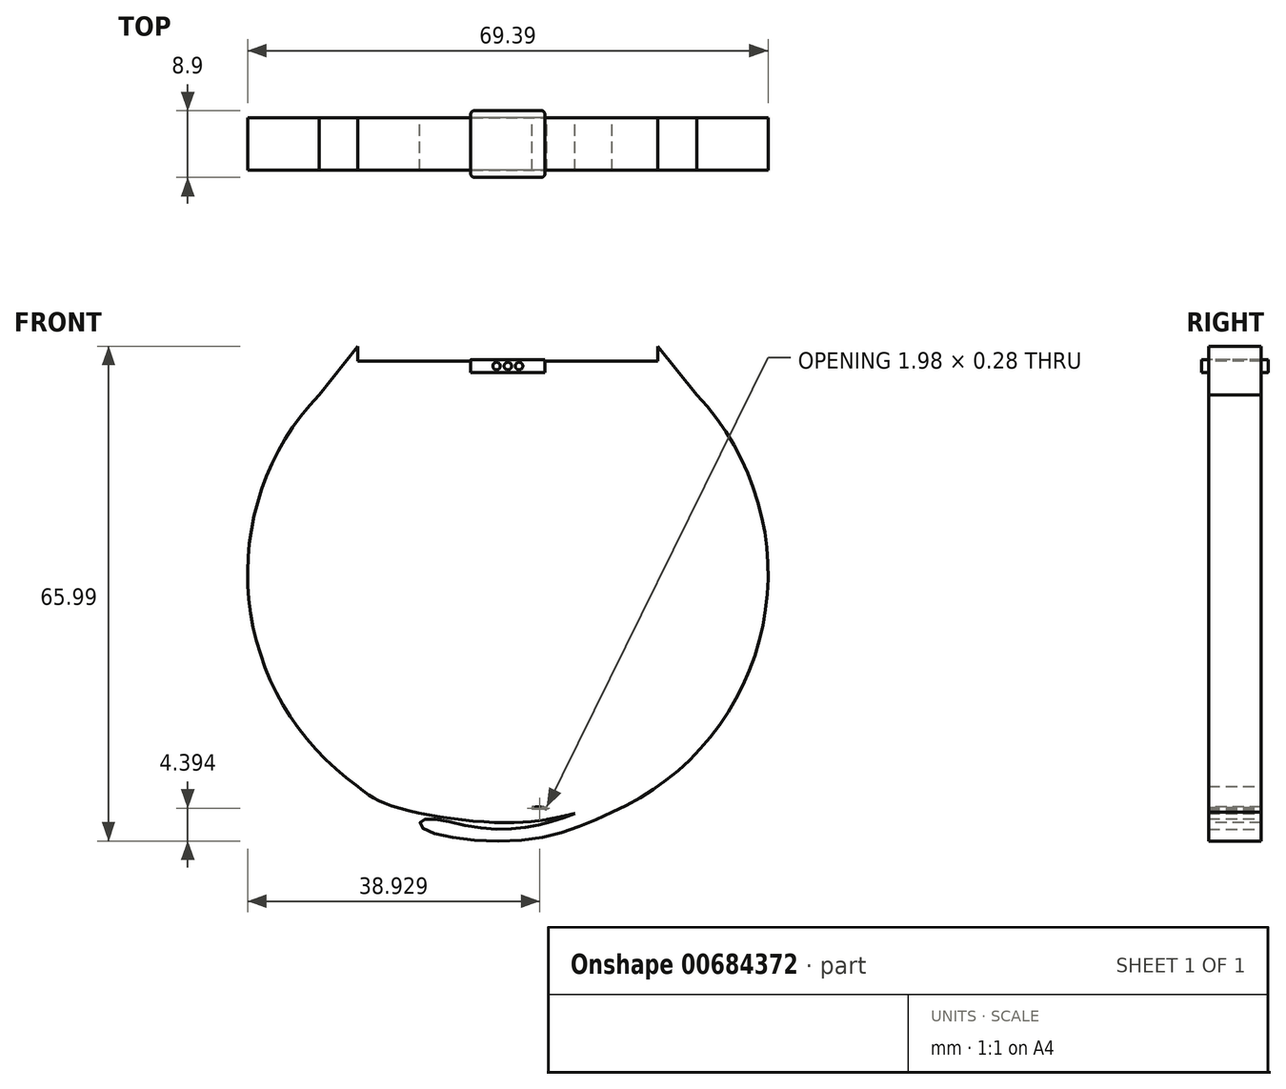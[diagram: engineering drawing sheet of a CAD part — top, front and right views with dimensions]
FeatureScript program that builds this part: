
annotation { "Feature Type Name" : "Feature", "Feature Type Description" : "" }
export const myFeature = defineFeature(function(context is Context, id is Id, definition is map)
    precondition{}
    {
        {
            var Q0;
            Q0=qCreatedBy(makeId("Front.planeOp"),FACE);
            var sketch = newSketch(context, id + "F0", { "sketchPlane" : qUnion([Q0])});
            skArc(sketch, "E0", {"start": v(-25.17, 23.88) * mm, "mid": v(-34.52, -3.42) * mm, "end": v(-20, -28.35) * mm});
            skLineSegment(sketch, "E1", {"start": v(-20, 28.35) * mm, "end": v(20, 28.35) * mm});
            skLineSegment(sketch, "E2.0", {"start": v(-19.52, 26.85) * mm, "end": v(19.52, 26.85) * mm});
            skArc(sketch, "E2.1", {"start": v(-19.52, 26.85) * mm, "mid": v(-33.2, 0.26) * mm, "end": v(-19.94, -26.54) * mm});
            skPoint(sketch, "E3.top.start.orphan", {"position": v(20, -28.35) * mm});
            skPoint(sketch, "E4.trimOffspring.end.orphan", {"position": v(-20, -28.35) * mm});
            skFitSpline(sketch, "E5", {"points": [v(8.98, -31.96) * mm, v(0, -33.2) * mm, v(-16.13, -30.72) * mm, v(-20, -28.35) * mm], "startDerivative": vector(-23.65, -5.7) * mm, "endDerivative": vector(-12.46, 10.4) * mm});
            skPoint(sketch, "E6.2.internal.orphan", {"position": v(0, -32) * mm});
            skFitSpline(sketch, "E7", {"points": [v(-19.94, -26.54) * mm, v(-15.76, -29.23) * mm, v(-6.5, -31.45) * mm, v(5.23, -31.39) * mm, v(6.4, -32.58) * mm], "startDerivative": vector(17.01, -12.6) * mm, "endDerivative": vector(5.13, -10.96) * mm});
            skArc(sketch, "E8.trimOffspring", {"start": v(13.9, -31.8) * mm, "mid": v(34.01, -6.89) * mm, "end": v(25.17, 23.88) * mm});
            skPoint(sketch, "E9.1.internal.orphan", {"position": v(-16.13, -31.87) * mm});
            skPoint(sketch, "E9.2.internal.orphan", {"position": v(0, -34.7) * mm});
            skArc(sketch, "E10.trimOffspring", {"start": v(8.98, -31.96) * mm, "mid": v(32.67, -5.86) * mm, "end": v(19.52, 26.85) * mm});
            skFitSpline(sketch, "E11", {"points": [v(5.13, -32.78) * mm, v(5.23, -31.39) * mm, v(3.25, -31.13) * mm], "startDerivative": vector(1.1, 3.62) * mm, "endDerivative": vector(-4.68, -0.25) * mm});
            skFitSpline(sketch, "E12", {"points": [v(8.98, -31.96) * mm, v(3.25, -33.67) * mm, v(-4.8, -33.73) * mm, v(-11.28, -32.78) * mm, v(-11.61, -33.67) * mm, v(1.12, -35.57) * mm, v(13.9, -31.8) * mm], "startDerivative": vector(-36, -13.01) * mm, "endDerivative": vector(49.5, 22.79) * mm});
            skLineSegment(sketch, "E13", {"start": v(20, 28.35) * mm, "end": v(20, 30.35) * mm});
            skLineSegment(sketch, "E14", {"start": v(20, 30.35) * mm, "end": v(25.17, 23.88) * mm});
            skLineSegment(sketch, "E15", {"start": v(25.17, 23.88) * mm, "end": v(-25.17, 23.88) * mm, "construction": true});
            skLineSegment(sketch, "E16", {"start": v(-20, 28.35) * mm, "end": v(-20, 30.35) * mm});
            skLineSegment(sketch, "E17", {"start": v(-20, 30.35) * mm, "end": v(-25.17, 23.88) * mm});
            skSolve(sketch);
        }
        {
            var Q0;
            Q0 = qSketchRegion(id + "F0", true);
            extrude(context, id + "F1", {"entities" : qUnion([Q0]), "depth" : 7 * mm, "offsetDistance" : 25 * mm});
        }
        {
            var Q0;
            Q0=makeQuery(id+"F1.opExtrude","SWEPT_FACE",FACE,{"disambiguationData":[OSD([sQuery(id+"F0.wireOp",EDGE,"E1")])]});
            var sketch = newSketch(context, id + "F2", { "sketchPlane" : qUnion([Q0])});
            skLineSegment(sketch, "E18", {"start": v(0, 0) * mm, "end": v(0, -7) * mm, "construction": true});
            skLineSegment(sketch, "E19.bottom", {"start": v(-4.95, 0.95) * mm, "end": v(4.95, 0.95) * mm});
            skLineSegment(sketch, "E19.top", {"start": v(-4.95, -7.95) * mm, "end": v(4.95, -7.95) * mm});
            skLineSegment(sketch, "E19.left", {"start": v(-4.95, 0.95) * mm, "end": v(-4.95, -7.95) * mm});
            skLineSegment(sketch, "E19.right", {"start": v(4.95, 0.95) * mm, "end": v(4.95, -7.95) * mm});
            skPoint(sketch, "E19.middle", {"position": v(0, -3.5) * mm});
            skSolve(sketch);
        }
        {
            var Q0;
            Q0 = qSketchRegion(id + "F2", true);
            extrude(context, id + "F3", {"entities" : qUnion([Q0]), "operationType" : NewBodyOperationType.ADD, "oppositeDirection" : true, "depth" : 1.5 * mm, "offsetDistance" : 25 * mm});
        }
        {
            var Q0;
            Q0 = qSketchRegion(id + "F2", true);
            extrude(context, id + "F4", {"entities" : qUnion([Q0]), "operationType" : NewBodyOperationType.ADD, "depth" : 0.2 * mm, "offsetDistance" : 25 * mm});
        }
        {
            var Q0;
            {var subQ0=sQuery(id+"F2.wireOp",EDGE,"E19.left");var subQ1=sQuery(id+"F2.wireOp",EDGE,"E19.top");Q0=makeQuery(id+"F4.boolean.opBoolean","MERGE",EDGE,{"derivedFrom":[makeQuery(id+"F3.opExtrude","SWEPT_EDGE",EDGE,{"disambiguationData":[OSD([subQ1,subQ0])]}),makeQuery(id+"F4.opExtrude","SWEPT_EDGE",EDGE,{"disambiguationData":[OSD([subQ1,subQ0])]})]});}
            var Q1;
            {var subQ0=sQuery(id+"F2.wireOp",EDGE,"E19.right");var subQ1=sQuery(id+"F2.wireOp",EDGE,"E19.top");Q1=makeQuery(id+"F4.boolean.opBoolean","MERGE",EDGE,{"derivedFrom":[makeQuery(id+"F3.opExtrude","SWEPT_EDGE",EDGE,{"disambiguationData":[OSD([subQ1,subQ0])]}),makeQuery(id+"F4.opExtrude","SWEPT_EDGE",EDGE,{"disambiguationData":[OSD([subQ1,subQ0])]})]});}
            var Q2;
            {var subQ0=sQuery(id+"F2.wireOp",EDGE,"E19.right");var subQ1=sQuery(id+"F2.wireOp",EDGE,"E19.bottom");Q2=makeQuery(id+"F4.boolean.opBoolean","MERGE",EDGE,{"derivedFrom":[makeQuery(id+"F3.opExtrude","SWEPT_EDGE",EDGE,{"disambiguationData":[OSD([subQ1,subQ0])]}),makeQuery(id+"F4.opExtrude","SWEPT_EDGE",EDGE,{"disambiguationData":[OSD([subQ1,subQ0])]})]});}
            var Q3;
            {var subQ0=sQuery(id+"F2.wireOp",EDGE,"E19.left");var subQ1=sQuery(id+"F2.wireOp",EDGE,"E19.bottom");Q3=makeQuery(id+"F4.boolean.opBoolean","MERGE",EDGE,{"derivedFrom":[makeQuery(id+"F3.opExtrude","SWEPT_EDGE",EDGE,{"disambiguationData":[OSD([subQ1,subQ0])]}),makeQuery(id+"F4.opExtrude","SWEPT_EDGE",EDGE,{"disambiguationData":[OSD([subQ1,subQ0])]})]});}
            fillet(context, id + "F5", {"entities" : qUnion([Q0, Q1, Q2, Q3]), "radius" : 0.5 * mm, "tangentPropagation" : true, "allowEdgeOverflow" : false});
        }
        {
            var Q0;
            {var subQ0=sQuery(id+"F2.wireOp",EDGE,"E19.top");Q0=makeQuery(id+"F4.boolean.opBoolean","MERGE",FACE,{"derivedFrom":[makeQuery(id+"F3.opExtrude","SWEPT_FACE",FACE,{"disambiguationData":[OSD([subQ0])]}),makeQuery(id+"F4.opExtrude","SWEPT_FACE",FACE,{"disambiguationData":[OSD([subQ0])]})]});}
            var sketch = newSketch(context, id + "F6", { "sketchPlane" : qUnion([Q0])});
            skLineSegment(sketch, "E20", {"start": v(0, 28.55) * mm, "end": v(0, 26.85) * mm, "construction": true});
            skCircle(sketch, "E21", {"center": v(0, 27.7) * mm, "radius": 0.5 * mm});
            skCircle(sketch, "E22.1.0.0", {"center": v(1.5, 27.7) * mm, "radius": 0.5 * mm});
            skLineSegment(sketch, "E22.direction1", {"start": v(0, 27.7) * mm, "end": v(1.5, 27.7) * mm, "construction": true});
            skCircle(sketch, "E23.1.0.0", {"center": v(-1.5, 27.7) * mm, "radius": 0.5 * mm});
            skLineSegment(sketch, "E23.direction1", {"start": v(0, 27.7) * mm, "end": v(-1.5, 27.7) * mm, "construction": true});
            skSolve(sketch);
        }
        {
            var Q0;
            Q0 = qSketchRegion(id + "F6", true);
            extrude(context, id + "F7", {"entities" : qUnion([Q0]), "operationType" : NewBodyOperationType.REMOVE, "oppositeDirection" : true, "depth" : 0.07 * mm, "offsetDistance" : 25 * mm});
        }
        {
            var Q0;
            Q0=makeQuery(id+"F7.boolean.opBoolean","COPY",EDGE,{"derivedFrom":makeQuery(id+"F7.opExtrude","CAP_EDGE",EDGE,{"disambiguationData":[OSD([sQuery(id+"F6.wireOp",EDGE,"E23.1.0.0")])],"isStart":false})});
            var Q1;
            Q1=makeQuery(id+"F7.boolean.opBoolean","COPY",EDGE,{"derivedFrom":makeQuery(id+"F7.opExtrude","CAP_EDGE",EDGE,{"disambiguationData":[OSD([sQuery(id+"F6.wireOp",EDGE,"E21")])],"isStart":false})});
            var Q2;
            Q2=makeQuery(id+"F7.boolean.opBoolean","COPY",EDGE,{"derivedFrom":makeQuery(id+"F7.opExtrude","CAP_EDGE",EDGE,{"disambiguationData":[OSD([sQuery(id+"F6.wireOp",EDGE,"E22.1.0.0")])],"isStart":false})});
            fillet(context, id + "F8", {"entities" : qUnion([Q0, Q1, Q2]), "radius" : 0.3 * mm, "tangentPropagation" : true, "allowEdgeOverflow" : false});
        }
    });
